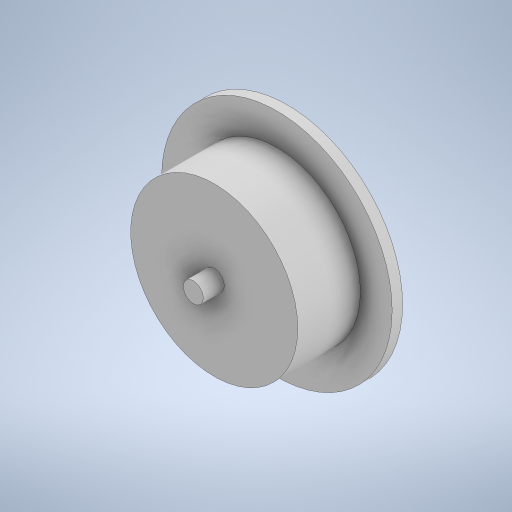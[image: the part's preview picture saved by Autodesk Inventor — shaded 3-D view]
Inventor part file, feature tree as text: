
AUTODESK INVENTOR PART (.ipt)
format: ipt  version: 2023 (Build 270158030, 158C)  size: 270,336 bytes
history: native  units: in
note: dims shown in document units (in); Inventor stores cm internally (conversion verified against a paired STEP export)
features: extrude x5, sketch x5
ambient origin geometry x8: Origin, YZ Plane, XZ Plane, XY Plane, X Axis, Y Axis, Z Axis, Center Point
bodies: Solid1 (feature_tree)
feature tree (10):
  extrude  "Extrusion1"  Depth=0.0625in TaperAngle=0.0deg
  extrude  "Extrusion2"  Depth=0.375in TaperAngle=0.0deg
  extrude  "Extrusion3"  Depth=0.0625in TaperAngle=0.0deg
  extrude  "Extrusion4"  Depth=0.125in TaperAngle=0.0deg
  extrude  "Extrusion5"  Depth=0.125in TaperAngle=0.0deg
  sketch  "Sketch1"  dims[d0=1.38in d1=0.0625in d2=0.0in]
  sketch  "Sketch2"  dims[d3=1.0in d4=0.375in d5=0.0in]
  sketch  "Sketch3"  dims[d6=0.581in d7=0.0625in d8=0.0in]
  sketch  "Sketch4"  dims[d9=0.281in d10=0.125in d11=0.0in]
  sketch  "Sketch5"  dims[d12=0.12in d13=0.125in d14=0.0in]
